# Revit family: Libra_V_28W_4000K_3780LM
name_source: partatom
category: Lighting Fixtures
units: mm (PartAtom-declared; Revit-internal decimal feet)

## family parameters
Always vertical = Yes
Cut with Voids When Loaded = No
Host = Ceiling
Light Source = Yes
OmniClass Number = 23.80.70.11
OmniClass Title = Luminaries for Internal Lighting
Part Type = Normal
Room Calculation Point = No
Round Connector Dimension = Use Diameter
Shared = No

## types (1)
- Type 1
    Alimentation Driver = AC 220-240V
    Alimentation luminaire = 700mA
    Angle d'éclairage = 360°
    Color Filter = 16777215
    Default Elevation = 0 mm  [stored 0 ft]
    Diffuseur = Satiné mat
    Dimensions = ø 100 mm; H : 1210 mm
    Dimming Lamp Color Temperature Shift = <None>
    Driver = Driver Osram (déporté 230V/CC) - 350mA
    Durée de vie = 50 000 heures
    Flux lumineux = 3780 lm
    IRC = >80
    Maintien du flux = L80B10 (50 000 heures)
    Matériau = Acrylique et embouts en aluminium
    Photometric Web File = google_eulumdat_converter (11).ies
    Puissance nominale = 28W
    SDCM = <3
    Température = 4000K (disponible en 3000K - sur demande)
    Tilt Angle = 90.00°
    Type = Suspension tubulaire
    Type de lampe = LED Samsung 2835 - 28W/m

note: [stored X ft] marks values corroborated as IEEE doubles in the binary element streams (Revit-internal decimal feet)

## geometry (parser evidence)
native form markers: Sweep x2
no freeform markers — native parametric forms only
